# Revit family: PG66
name_source: partatom
category: Equipement spécialisé
units: mm (PartAtom-declared; Revit-internal decimal feet)

## family parameters
Autoriser la découpe dans les vues = Non
Basée sur le plan de construction = Non
Conserver l'orientation des annotations = Non
Cote de connecteur circulaire = Utiliser le diamètre
Couper avec des vides une fois chargée = Non
Numéro OmniClass = 23.40.40.14
Partagée = Non
Repère de localisation dans la pièce = Non
Titre OmniClass = Food Service Equipment
Toujours verticalement = Oui
Type d'élément = Normal

## types (4) — shared parameters
Altezza allacciamento elettrico da pavimento finito = 135 mm  [stored 0.442913 ft]
Altezza da terra raccordo acqua calda = 175 mm  [stored 0.574147 ft]
Altezza dello scarico diretto acqua da pavimento finito = 145 mm  [stored 0.475722 ft]
Corrente di funzionamento normale = 14 A
Description = THREE-PHASE FRONT LOADING POTWASHER WITH RCD
Diametro dello scarico diretto di acqua = 1 1/2"
Diametro raccordo acqua calda = 1"
Fabricant = COMENDA
Fase = 3
Frequenza = 50 Hz
Numero dei poli = 3
Peso netto = 200.00 kg
Pessione minima acqua fredda = 200000.0 Pa
Potenza elettrica = 9000 W
Pressione minima acqua calda = 200000.0 Pa
Protezione contro le sovracorrenti = 16 A
Temperatura raccomandata per acqua calda = 50 °C
Tensione = 400 V
URL = www.comenda.eu
URL catalogo = https://comenda.eu
zero-valued in all types: Elévation par défaut

## per-type parameters (varying)
| type | Altezza | Lunghezza | Modèle | Profondità |
| 6G3257 | 1915 mm  [stored 6.28281 ft] | 840 mm  [stored 2.75591 ft] | G-EVO 605H R RCD | 870 mm  [stored 2.85433 ft] |
| 6G3150 | 1870 mm | 860 mm | G-EVO 605 R RCD | 900 mm  [stored 2.95276 ft] |
| 6G3180 | 1870 mm | 860 mm | G-EVO 655 R RCD | 900 mm  [stored 2.95276 ft] |
| 6G3185 | 2020 mm  [stored 6.6273 ft] | 860 mm | G-EVO 655H R RCD | 900 mm  [stored 2.95276 ft] |

note: [stored X ft] marks values corroborated as IEEE doubles in the binary element streams (Revit-internal decimal feet)

## geometry (parser evidence)
native form markers: Sweep x4
no freeform markers — native parametric forms only
